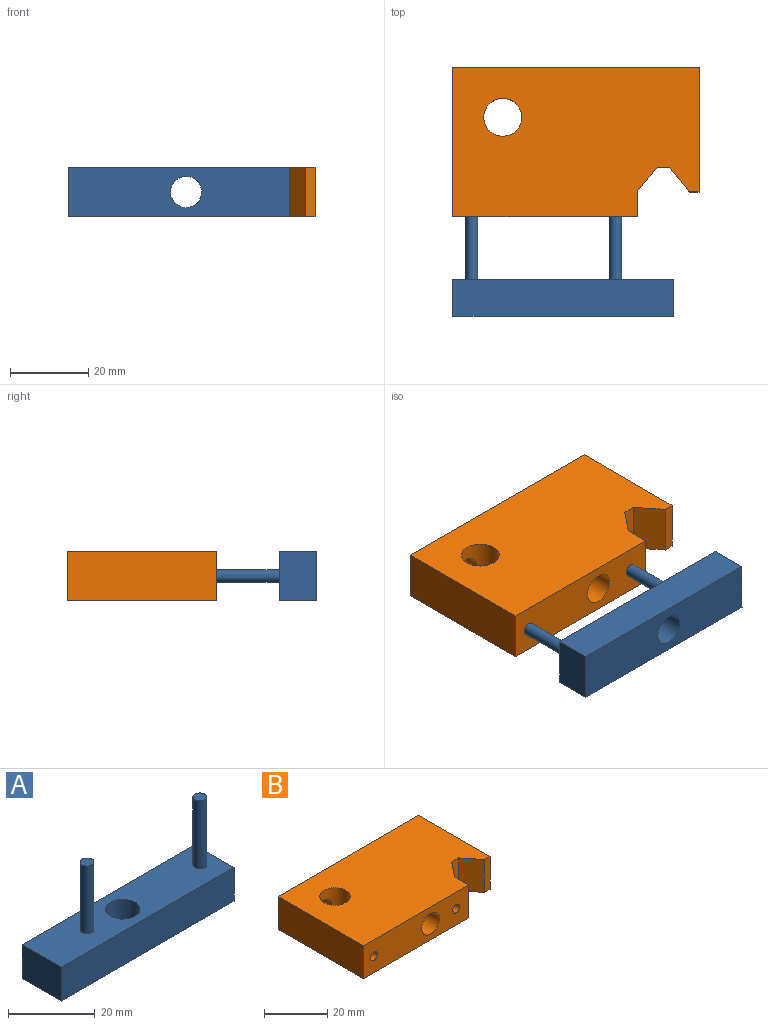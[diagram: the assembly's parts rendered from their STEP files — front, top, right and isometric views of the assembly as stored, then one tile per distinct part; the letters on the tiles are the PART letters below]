
ASSEMBLY  parts=2 mates=1
PART A: 11 faces, bbox 56.3x12.7x28.6 mm
  f0: plane 12.7x9.53mm, normal (1,0,0), area 121mm2, adj f1,f3,f5,f6
  f1: plane 56.29x9.53mm, normal (0,1,0), area 536.1mm2, adj f0,f2,f5,f6
  f2: plane 12.7x9.53mm, normal (-1,0,0), area 121mm2, adj f1,f3,f5,f6
  f3: plane 56.29x9.53mm, normal (0,-1,0), area 536.1mm2, adj f0,f2,f5,f6
  f4: cylinder r=3.97mm len=9.53mm, axis (0,0,-1), area 237.5mm2, adj f5,f6
  f5: plane 56.29x12.7mm, normal (0,0,1), area 649.5mm2, adj f0,f1,f2,f3,f4,f7,f9
  f6: plane 56.29x12.7mm, normal (0,0,-1), area 665.4mm2, adj f0,f1,f2,f3,f4
  f7: cylinder r=1.59mm len=19.05mm, axis (0,0,-1), area 190mm2, adj f5,f8
  f8: plane 3.18x3.18mm, normal (0,0,1), area 7.9mm2, adj f7
  f9: cylinder r=1.59mm len=19.05mm, axis (0,0,-1), area 190mm2, adj f5,f10
  f10: plane 3.18x3.18mm, normal (0,0,1), area 7.9mm2, adj f9
PART B: 16 faces, bbox 62.8x38.1x12.7 mm
  f0: plane 12.7x2.46mm, normal (0,-1,0), area 31.3mm2, adj f1,f9,f10,f11
  f1: plane 31.75x12.7mm, normal (1,0,0), area 403.2mm2, adj f0,f2,f10,f11
  f2: plane 62.79x12.7mm, normal (0,1,0), area 709.5mm2, adj f1,f3,f10,f11,f12,f13,f14,f15
  f3: plane 38.1x12.7mm, normal (-1,0,0), area 483.9mm2, adj f2,f4,f10,f11
  f4: plane 46.99x12.7mm, normal (0,-1,0), area 531.5mm2, adj f3,f5,f10,f11,f13,f14,f15
  f5: plane 12.7x6.35mm, normal (1,0,0), area 80.6mm2, adj f4,f6,f10,f11
  f6: plane 12.7x6.35mm, normal (0.78,-0.62,0), area 103.3mm2, adj f5,f7,f10,f11
  f7: plane 12.7x3.18mm, normal (0,-1,0), area 40.3mm2, adj f6,f9,f10,f11
  f8: cylinder r=4.83mm len=12.7mm, axis (0,0,-1), area 361.6mm2, adj f10,f11,f12
  f9: plane 12.7x6.35mm, normal (-0.78,-0.62,0), area 103.3mm2, adj f0,f7,f10,f11
  f10: plane 62.79x38.1mm, normal (0,0,1), area 2166.3mm2, adj f0,f1,f2,f3,f4,f5,f6,f7
  f11: plane 62.79x38.1mm, normal (0,0,-1), area 2166.3mm2, adj f0,f1,f2,f3,f4,f5,f6,f7
  f12: cylinder r=2.68mm len=8.69mm, axis (0,1,0), area 139.3mm2, adj f2,f8
  f13: cylinder r=1.59mm len=38.1mm, axis (0,-1,0), area 380mm2, adj f2,f4
  f14: cylinder r=3.97mm len=38.1mm, axis (0,-1,0), area 950.1mm2, adj f2,f4
  f15: cylinder r=1.59mm len=38.1mm, axis (0,-1,0), area 380mm2, adj f2,f4
PLACE A rot(axis=(0,0.71,0.71),180deg) t=(-12.12,-178.04,47.77)mm
PLACE B rot(axis=(-0.86,0.2,-0.47),0deg) t=(23.24,-152.64,41.42)mm
MATE slider B.f13 <-> A.f7  axis (0,-1,0) through (1.19,-152.64,47.77)mm
